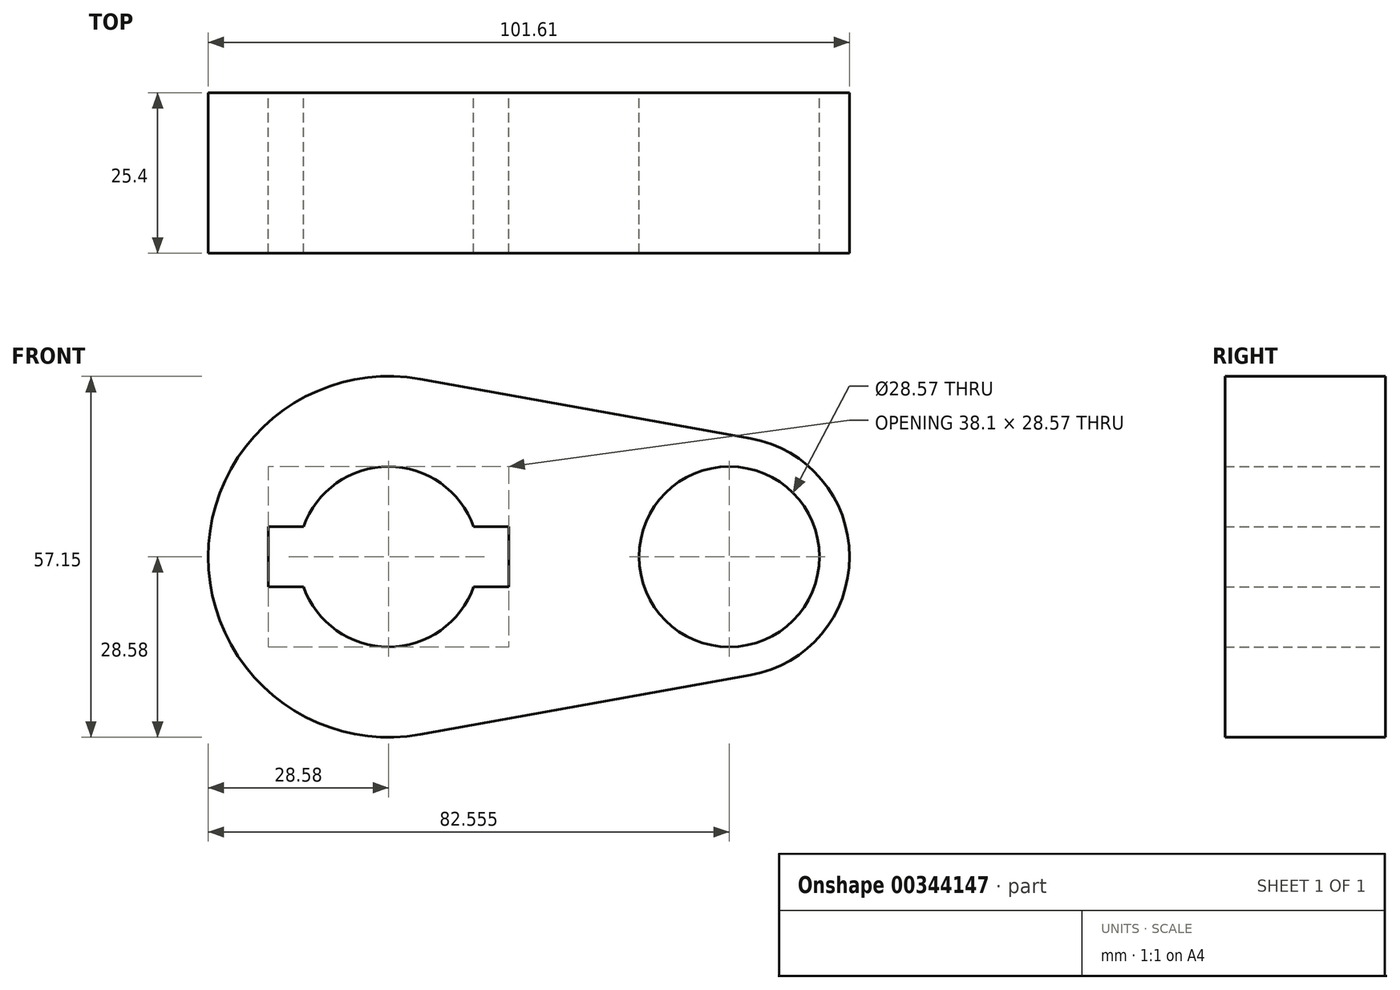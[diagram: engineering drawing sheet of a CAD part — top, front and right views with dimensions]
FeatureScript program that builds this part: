
annotation { "Feature Type Name" : "Feature", "Feature Type Description" : "" }
export const myFeature = defineFeature(function(context is Context, id is Id, definition is map)
    precondition{}
    {
        {
            var Q0;
            Q0=qCreatedBy(makeId("Front.planeOp"),FACE);
            var sketch = newSketch(context, id + "F0", { "sketchPlane" : qUnion([Q0])});
            skCircle(sketch, "E0", {"center": v(0, 0) * mm, "radius": 28.58 * mm});
            skCircle(sketch, "E1", {"center": v(53.98, 0) * mm, "radius": 19.05 * mm});
            skLineSegment(sketch, "E2", {"start": v(5.04, 28.13) * mm, "end": v(57.34, 18.75) * mm});
            skLineSegment(sketch, "E3", {"start": v(5.04, -28.13) * mm, "end": v(57.34, -18.75) * mm});
            skCircle(sketch, "E4", {"center": v(0, 0) * mm, "radius": 14.29 * mm});
            skCircle(sketch, "E5", {"center": v(53.98, 0) * mm, "radius": 14.29 * mm});
            skLineSegment(sketch, "E6.bottom", {"start": v(-19.05, 4.76) * mm, "end": v(19.05, 4.76) * mm});
            skLineSegment(sketch, "E6.top", {"start": v(-19.05, -4.76) * mm, "end": v(19.05, -4.76) * mm});
            skLineSegment(sketch, "E6.left", {"start": v(-19.05, 4.76) * mm, "end": v(-19.05, -4.76) * mm});
            skLineSegment(sketch, "E6.right", {"start": v(19.05, 4.76) * mm, "end": v(19.05, -4.76) * mm});
            skSolve(sketch);
        }
        {
            var Q0;
            {var subQ7=sQuery(id+"F0.wireOp",EDGE,"E6.left");Q0=makeQuery(id+"F0.imprint","IMPRINT",FACE,{"disambiguationData":[TD([[makeQuery(id+"F0.imprint","IMPRINT",EDGE,{"derivedFrom":subQ7}),-1.0]])]});}
            var Q1;
            {var subQ0=sQuery(id+"F0.wireOp",EDGE,"E2");Q1=makeQuery(id+"F0.imprint","IMPRINT",FACE,{"disambiguationData":[TD([[makeQuery(id+"F0.imprint","IMPRINT",EDGE,{"derivedFrom":subQ0}),-1.0]])]});}
            var Q2;
            Q2=makeQuery(id+"F0.imprint","IMPRINT",FACE,{"disambiguationData":[TD([[makeQuery(id+"F0.imprint","IMPRINT",EDGE,{"derivedFrom":sQuery(id+"F0.wireOp",EDGE,"E5")}),-1.0]])]});
            extrude(context, id + "F1", {"entities" : qUnion([Q0, Q1, Q2]), "depth" : 25.4 * mm});
        }
    });
